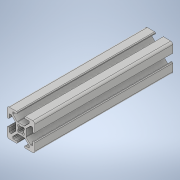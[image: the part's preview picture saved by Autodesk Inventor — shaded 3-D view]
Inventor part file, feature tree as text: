
AUTODESK INVENTOR PART (.ipt)
format: ipt  version: 2022 (Build 260153000, 153)  size: 245,760 bytes
history: native  units: mm
features: plane x2, extrude x1, sketch x1
ambient origin geometry x8: Origin, YZ Plane, XZ Plane, XY Plane, X Axis, Y Axis, Z Axis, Center Point
bodies: Solid1 (feature_tree)
feature tree (4):
  extrude  "Extrusion1"  [1 undecoded]
  plane  "Work Plane1"
  plane  "Work Plane2"
  sketch  "Sketch_1"  dims[d0=100.0mm d1=0.0mm]
note: 1 required parameter value undecoded (feature->parameter linkage not recoverable at this tier; creation-order binding heuristic only, values carry confidence <= 0.55)
